# Revit family: Roof-Hatch_Best-Access-Doors_Galvannealed-BA-RHT
name_source: partatom
category: Specialty Equipment
units: mm (PartAtom-declared; Revit-internal decimal feet)

## family parameters
Cut with Voids When Loaded = No
Host = Face
OmniClass Number = 23.30.10.27.24
Part Type = Normal
Room Calculation Point = No
Round Connector Dimension = Use Diameter
Shared = No

## types (3) — shared parameters
Assembly Code = C1020700
Construction Material = Metal - Best Access Doors - Aluminum
Default Elevation = 0"
Description = Roof hatch
Finish = Metal - Best Access Doors - Powder Coated White
Height = 12"
Manufacturer = Best Access Doors
Product Page URL = https://www.bestaccessdoors.com
Product data url = https://bimobject.com
URL = https://www.bestaccessdoors.com

## per-type parameters (varying)
| type | Door Height | Door Width | Frame Height | Frame Width | Model |
| Custom | 48" | 48" | 49 11/32" | 49 29/32" |  |
| 36 x 30 | 30" | 36" | 31 11/32" | 37 29/32" | BA-RHT-36-30 |
| 36 x 36 | 36" | 36" | 37 11/32" | 37 29/32" | BA-RHT-36-36 |

## geometry (parser evidence)
native form markers: Blend x2, Sweep x7
no freeform markers — native parametric forms only
